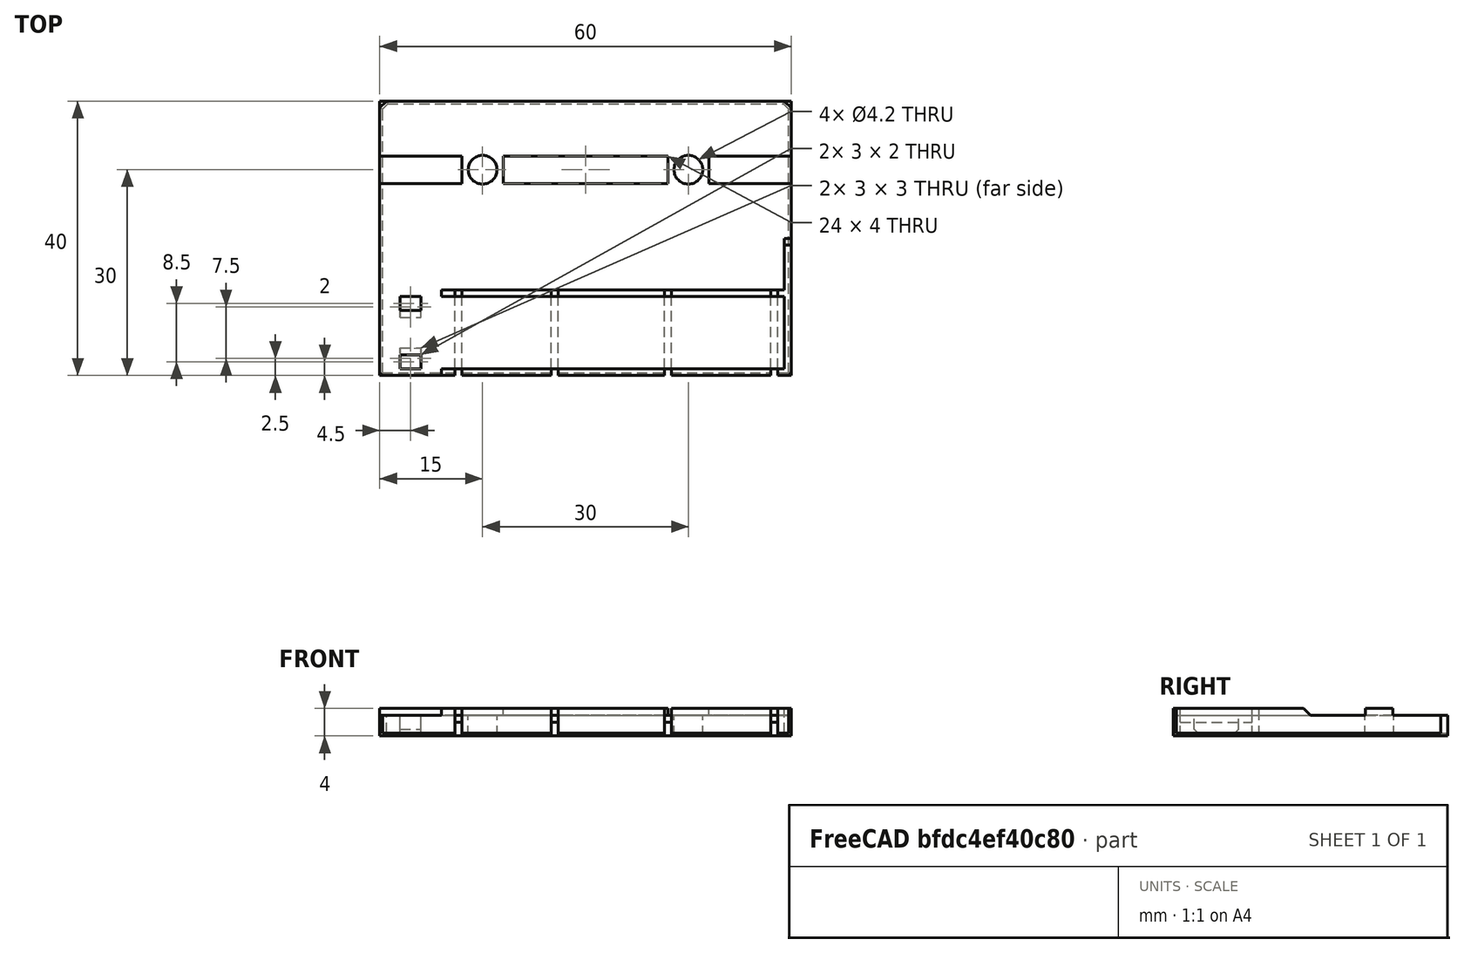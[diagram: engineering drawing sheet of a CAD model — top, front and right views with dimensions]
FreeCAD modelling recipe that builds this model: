
FCSTD DOCUMENT  (FreeCAD 0.18R16146 (Git))
Label: neopixel-mount-3
License: All rights reserved
LicenseURL: http://en.wikipedia.org/wiki/All_rights_reserved
objects: Part::Box×22, Part::MultiFuse×6, Part::Chamfer×4, Part::Cut×3, Part::Cylinder×2, Part::Feature×1
note: 38 computed .brp shape members not serialized (recipe doc carries the construction recipe); baked Part::Feature solids carry a one-line shape summary decoded from their .brp

FEATURE [Part::Box] Box  label="Cube"
  AttacherType = Attacher::AttachEngine3D
  Height = 3
  Length = 60
  Width = 20
FEATURE [Part::Box] Box001  label="Cube001"
  AttacherType = Attacher::AttachEngine3D
  Height = 3
  Length = 60
  Placement = pos=(0,-20,0) rot=(0,0,1;0rad)
  Width = 20
FEATURE [Part::Box] Box002  label="Cube002"
  AttacherType = Attacher::AttachEngine3D
  Height = 4
  Length = 12
  Placement = pos=(0,8,0) rot=(0,0,1;0rad)
  Width = 4
FEATURE [Part::Cylinder] Cylinder
  Angle = 360
  AttacherType = Attacher::AttachEngine3D
  Height = 10
  Placement = pos=(15,10,0) rot=(0,0,1;0rad)
  Radius = 2.1
FEATURE [Part::Cylinder] Cylinder001
  Angle = 360
  AttacherType = Attacher::AttachEngine3D
  Height = 10
  Placement = pos=(45,10,0) rot=(0,0,1;0rad)
  Radius = 2.1
FEATURE [Part::Box] Box003  label="Cube003"
  AttacherType = Attacher::AttachEngine3D
  Height = 4
  Length = 12
  Placement = pos=(48,8,0) rot=(0,0,1;0rad)
  Width = 4
FEATURE [Part::Box] Box004  label="Cube004"
  AttacherType = Attacher::AttachEngine3D
  Height = 4
  Length = 24
  Placement = pos=(18,8,0) rot=(0,0,1;0rad)
  Width = 4
FEATURE [Part::MultiFuse] Fusion
  Shapes = -> [Box,Box002,Box004,Box003]
FEATURE [Part::MultiFuse] Fusion001
  Shapes = -> [Cylinder,Cylinder001]
FEATURE [Part::Cut] Cut
  Base = -> Fusion
  Tool = -> Fusion001
FEATURE [Part::Box] Box005  label="Cube005"
  AttacherType = Attacher::AttachEngine3D
  Height = 4
  Length = 50
  Placement = pos=(9,-20,0) rot=(0,0,1;0rad)
  Width = 1
FEATURE [Part::Box] Box006  label="Cube006"
  AttacherType = Attacher::AttachEngine3D
  Height = 4
  Length = 50
  Placement = pos=(9,-8.5,0) rot=(0,0,1;0rad)
  Width = 1
FEATURE [Part::Box] Box007  label="Cube007"
  AttacherType = Attacher::AttachEngine3D
  Height = 4
  Length = 1
  Placement = pos=(59,-20,0) rot=(0,0,1;0rad)
  Width = 20
FEATURE [Part::Box] Box008  label="Cube008"
  AttacherType = Attacher::AttachEngine3D
  Height = 8
  Length = 1
  Placement = pos=(11,-20,0) rot=(0,0,1;0rad)
  Width = 1
FEATURE [Part::Box] Box009  label="Cube009"
  AttacherType = Attacher::AttachEngine3D
  Height = 8
  Length = 1
  Placement = pos=(25,-20,0) rot=(0,0,1;0rad)
  Width = 1
FEATURE [Part::Box] Box010  label="Cube010"
  AttacherType = Attacher::AttachEngine3D
  Height = 8
  Length = 1
  Placement = pos=(41.5,-20,0) rot=(0,0,1;0rad)
  Width = 1
FEATURE [Part::Box] Box011  label="Cube011"
  AttacherType = Attacher::AttachEngine3D
  Height = 8
  Length = 1
  Placement = pos=(57,-20,0) rot=(0,0,1;0rad)
  Width = 1
FEATURE [Part::Box] Box012  label="Cube012"
  AttacherType = Attacher::AttachEngine3D
  Height = 8
  Length = 1
  Placement = pos=(25,-8.5,0) rot=(0,0,1;0rad)
  Width = 1
FEATURE [Part::Box] Box013  label="Cube013"
  AttacherType = Attacher::AttachEngine3D
  Height = 8
  Length = 1
  Placement = pos=(41.5,-8.5,0) rot=(0,0,1;0rad)
  Width = 1
FEATURE [Part::Box] Box014  label="Cube014"
  AttacherType = Attacher::AttachEngine3D
  Height = 8
  Length = 1
  Placement = pos=(11,-8.5,0) rot=(0,0,1;0rad)
  Width = 1
FEATURE [Part::Box] Box015  label="Cube015"
  AttacherType = Attacher::AttachEngine3D
  Height = 8
  Length = 1
  Placement = pos=(57,-8.5,0) rot=(0,0,1;0rad)
  Width = 1
FEATURE [Part::Chamfer] Chamfer
  Base = -> Box007
  Edges = 1 edges r=1: [Edge12]
FEATURE [Part::Box] Box019  label="Cube019"
  AttacherType = Attacher::AttachEngine3D
  Height = 10
  Length = 3
  Placement = pos=(3,-19,0) rot=(0,0,1;0rad)
  Width = 2
FEATURE [Part::Box] Box020  label="Cube020"
  AttacherType = Attacher::AttachEngine3D
  Height = 10
  Length = 3
  Placement = pos=(3,-10.5,0) rot=(0,0,1;0rad)
  Width = 2
FEATURE [Part::MultiFuse] Fusion002
  Shapes = -> [Box001,Box006,Box005,Chamfer]
FEATURE [Part::MultiFuse] Fusion003
  Shapes = -> [Box019,Box020,Box014,Box008,Box009,Box012,Box013,Box010,Box011,Box015]
FEATURE [Part::Cut] Cut001
  Base = -> Fusion002
  Tool = -> Fusion003
FEATURE [Part::Chamfer] Chamfer001
  Base = -> Cut001
  Edges = 2 edges r=1: [Edge84,Edge86]
FEATURE [Part::MultiFuse] Fusion004
  Shapes = -> [Cut,Chamfer001]
FEATURE [Part::Feature] Fusion004001  label="Fusion005"
  shape: bbox 60 x 40 x 4 mm, 92 faces (baked)
FEATURE [Part::Chamfer] Chamfer002
  Base = -> Fusion004001
  Edges = 2 edges r=1: [Edge13,Edge18]
FEATURE [Part::Box] Box021  label="Cube021"
  AttacherType = Attacher::AttachEngine3D
  Height = 2
  Length = 1
  Placement = pos=(11,-20,0) rot=(0,0,1;0rad)
  Width = 12
FEATURE [Part::Box] Box022  label="Cube022"
  AttacherType = Attacher::AttachEngine3D
  Height = 2
  Length = 1
  Placement = pos=(25,-20,0) rot=(0,0,1;0rad)
  Width = 12
FEATURE [Part::Box] Box023  label="Cube023"
  AttacherType = Attacher::AttachEngine3D
  Height = 2
  Length = 1
  Placement = pos=(41.5,-20,0) rot=(0,0,1;0rad)
  Width = 12
FEATURE [Part::Box] Box024  label="Cube024"
  AttacherType = Attacher::AttachEngine3D
  Height = 2
  Length = 1
  Placement = pos=(57,-20,0) rot=(0,0,1;0rad)
  Width = 12
FEATURE [Part::MultiFuse] Fusion004002
  Shapes = -> [Box024,Box021,Box023,Box022]
FEATURE [Part::Cut] Cut002
  Base = -> Chamfer002
  Tool = -> Fusion004002
FEATURE [Part::Chamfer] Chamfer003
  Base = -> Cut002
  Edges = 12 edges r=0.4: [Edge4,Edge6,Edge67,Edge71,Edge81,Edge91,Edge101,Edge111,Edge112,Edge113,Edge114,Edge133]
